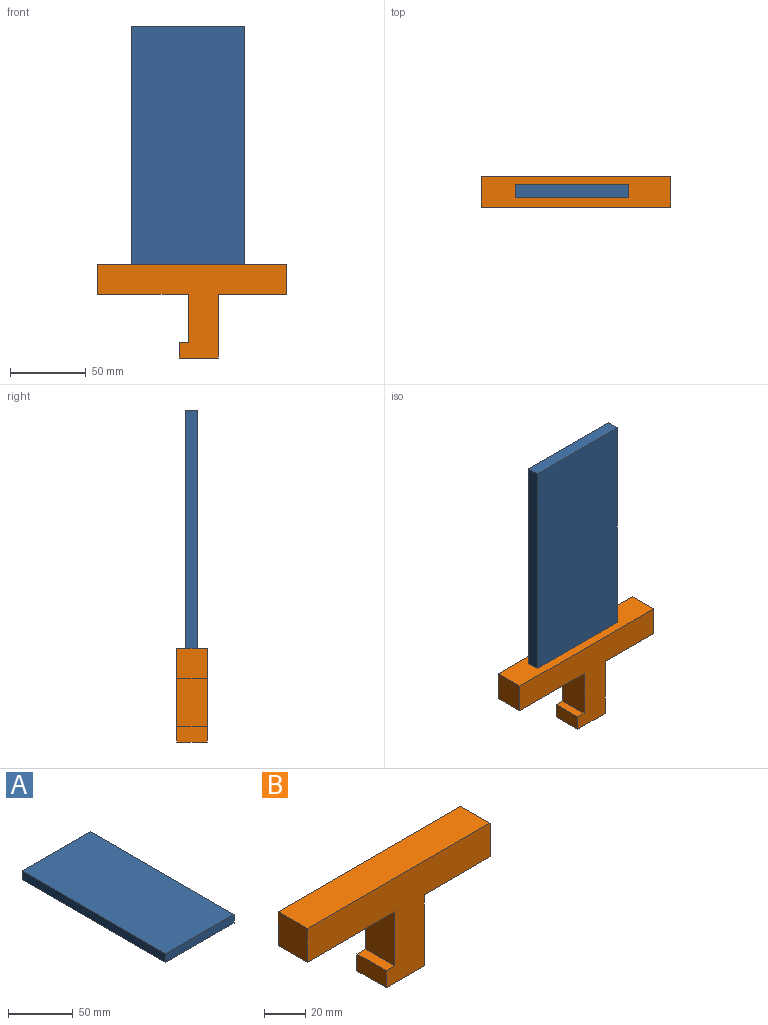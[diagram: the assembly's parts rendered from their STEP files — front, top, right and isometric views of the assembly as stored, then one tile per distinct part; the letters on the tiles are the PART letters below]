
ASSEMBLY  parts=2 mates=1
PART A: 6 faces, bbox 74.8x157.5x8.2 mm
  f0: plane 74.8x8.2mm, normal (0,-1,0), area 613.4mm2, adj f1,f3,f4,f5
  f1: plane 157.5x8.2mm, normal (1,0,0), area 1291.5mm2, adj f0,f2,f4,f5
  f2: plane 74.8x8.2mm, normal (0,1,0), area 613.4mm2, adj f1,f3,f4,f5
  f3: plane 157.5x8.2mm, normal (-1,0,0), area 1291.5mm2, adj f0,f2,f4,f5
  f4: plane 157.5x74.8mm, normal (0,0,1), area 11781mm2, adj f0,f1,f2,f3
  f5: plane 157.5x74.8mm, normal (0,0,-1), area 11781mm2, adj f0,f1,f2,f3
PART B: 12 faces, bbox 125x20x62 mm
  f0: plane 60x20mm, normal (0,0,-1), area 1200mm2, adj f1,f9,f10,f11
  f1: plane 32x20mm, normal (-1,0,0), area 640mm2, adj f0,f2,f10,f11
  f2: plane 20x6mm, normal (0,0,1), area 120mm2, adj f1,f3,f10,f11
  f3: plane 20x10mm, normal (-1,0,0), area 200mm2, adj f2,f4,f10,f11
  f4: plane 26x20mm, normal (0,0,-1), area 520mm2, adj f3,f5,f10,f11
  f5: plane 42x20mm, normal (1,0,0), area 840mm2, adj f4,f6,f10,f11
  f6: plane 45x20mm, normal (0,0,-1), area 900mm2, adj f5,f7,f10,f11
  f7: plane 20x20mm, normal (1,0,0), area 400mm2, adj f6,f8,f10,f11
  f8: plane 125x20mm, normal (0,0,1), area 2500mm2, adj f7,f9,f10,f11
  f9: plane 20x20mm, normal (-1,0,0), area 400mm2, adj f0,f8,f10,f11
  f10: plane 125x62mm, normal (0,-1,0), area 3400mm2, adj f0,f1,f2,f3,f4,f5,f6,f7
  f11: plane 125x62mm, normal (0,1,0), area 3400mm2, adj f0,f1,f2,f3,f4,f5,f6,f7
PLACE A rot(axis=(1,0,0),90deg) t=(-0.17,-5.63,98.75)mm
PLACE B at identity fixed
MATE planar A.f0 <-> B.f8  axis (0,0,-1) through (-0.17,-9.73,20)mm
